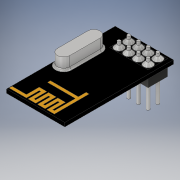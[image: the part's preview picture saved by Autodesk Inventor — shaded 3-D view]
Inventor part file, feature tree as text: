
AUTODESK INVENTOR PART (.ipt)
format: ipt  version: 2019.2 (Build 232265000, 265)  size: 291,840 bytes
history: native  units: mm
features: extrude x5, chamfer x2, emboss x2, fillet x1
ambient origin geometry x8: Origin, YZ Plane, XZ Plane, XY Plane, X Axis, Y Axis, Z Axis, Center Point
bodies: Solid1 (feature_tree)
feature tree (10):
  extrude  "Extrusion1"  Depth=28.0mm
  extrude  "Extrusion2"  Depth=15.0mm
  fillet  "Fillet1"  Radius=11.0mm
  extrude  "Extrusion5"  Depth=3.2mm
  chamfer  "Chamfer2"  Distance=0.5mm
  extrude  "Extrusion3"  Depth=6.0mm
  chamfer  "Chamfer1"  Distance=10.0mm
  extrude  "Extrusion4"  Depth=5.0mm
  emboss  "Emboss2"
  emboss  "Emboss1"
